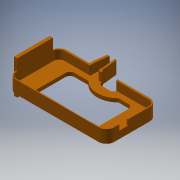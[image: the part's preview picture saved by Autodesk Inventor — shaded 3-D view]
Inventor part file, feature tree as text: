
AUTODESK INVENTOR PART (.ipt)
format: ipt  version: 2017 (Build 210142000, 142)  size: 366,592 bytes
history: native  units: in
note: dims shown in document units (in); Inventor stores cm internally (conversion verified against a paired STEP export)
features: extrude x13, sketch x13, fillet x9, projected_geometry x3, thicken_offset x1
ambient origin geometry x8: Origin, YZ Plane, XZ Plane, XY Plane, X Axis, Y Axis, Z Axis, Center Point
bodies: Solid1 (feature_tree)
feature tree (39):
  extrude  "Extrusion1"  Depth=2.655in
  extrude  "Extrusion2"  Depth=0.5in TaperAngle=0.0deg
  fillet  "Fillet1"  Radius=0.2in
  fillet  "Fillet2"  Radius=0.3in
  extrude  "Extrusion3"  Depth=0.42in
  extrude  "Extrusion4"  Depth=0.125in
  extrude  "Extrusion5"  Depth=0.125in
  fillet  "Fillet3"  Radius=0.125in
  fillet  "Fillet4"  Radius=0.125in
  fillet  "Fillet5"  Radius=0.125in
  extrude  "Extrusion6"  Depth=0.125in TaperAngle=0.0deg
  fillet  "Fillet6"  Radius=0.06in
  extrude  "Extrusion8"  Depth=0.04in
  fillet  "Fillet7"  Radius=0.25in
  extrude  "Extrusion10"  TaperAngle=0.0deg  [1 undecoded]
  extrude  "Extrusion11"  Depth=0.16in TaperAngle=0.0deg
  extrude  "Extrusion13"  Depth=1.1887in
  thicken_offset  "Thicken1"
  extrude  "Extrusion14"  Depth=0.9in
  sketch  "Sketch15"  dims[d57=0.25in d58=1.0in d59=0.0in d61=0.8in d62=0.48in d63=0.88in d64=0.3in d65=0.0in d66=2.0in d67=0.0in d72=0.0in d73=0.0in d74=0.875in d75=1.0in d77=0.04in d78=1.0in d79=0.0in d80=0.5in d81=0.5in d82=0.1in d83=0.0in d88=0.18in d89=0.14in d92=0.1in d93=0.625in d94=1.25in d95=0.0in d96=0.0in d97=0.125in]
  fillet  "Fillet10"  Radius=0.9in
  extrude  "Extrusion17"  Depth=0.3in
  fillet  "Fillet11"  Radius=0.3in
  extrude  "Extrusion12"  Depth=0.125in TaperAngle=0.0deg
  sketch  "Sketch1"  dims[d0=5.265in d1=2.655in]
  sketch  "Sketch2"  dims[d2=0.08in d3=0.5in d4=0.0in d5=0.2in d6=0.0in d7=0.3in]
  sketch  "Sketch3"  dims[d8=0.425in d9=0.42in]
  sketch  "Sketch4"  dims[d10=0.125in d11=0.0in d14=0.2275in]
  sketch  "Sketch5"  dims[d15=0.9in d17=0.125in d18=0.125in d19=0.125in d20=0.125in]
  sketch  "Sketch6"  dims[d21=0.0in d22=0.0in d23=0.125in d24=0.0in d25=0.06in]
  sketch  "Sketch8"  dims[d26=0.06in d27=0.04in d29=0.25in]
  sketch  "Sketch10"  dims[d30=2.75in d31=0.0in d32=0.0in]
  sketch  "Sketch11"  dims[d33=0.16in d43=1.0in d44=0.0in]
  sketch  "Sketch12"  dims[d45=1.1887in d46=1.1887in]
  sketch  "Sketch13"  dims[d47=0.2549in d50=1.932in d53=0.9in]
  sketch  "Sketch14"  dims[d54=0.9in d55=0.3in d56=0.3in]
  projected_geometry  "Projected Loop1"
  projected_geometry  "Projected Loop2"
  projected_geometry  "Projected Loop3"
note: 1 required parameter value undecoded (feature->parameter linkage not recoverable at this tier; creation-order binding heuristic only, values carry confidence <= 0.55)
